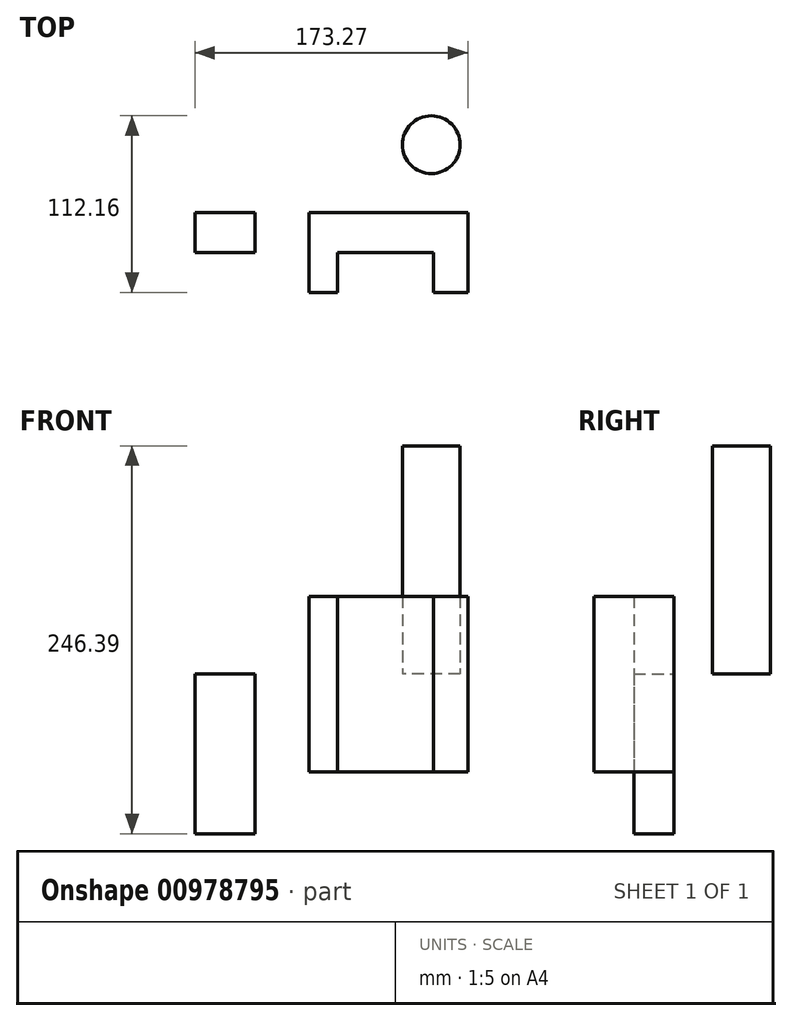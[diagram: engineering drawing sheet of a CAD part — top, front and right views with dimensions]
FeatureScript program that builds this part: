
annotation { "Feature Type Name" : "Feature", "Feature Type Description" : "" }
export const myFeature = defineFeature(function(context is Context, id is Id, definition is map)
    precondition{}
    {
        {
            var Q0;
            Q0=qCreatedBy(makeId("Front.planeOp"),FACE);
            var sketch = newSketch(context, id + "F0", { "sketchPlane" : qUnion([Q0])});
            skLineSegment(sketch, "E0.bottom", {"start": v(-48.02, 49.2) * mm, "end": v(52.96, 49.2) * mm});
            skLineSegment(sketch, "E0.top", {"start": v(-48.02, -62.25) * mm, "end": v(52.96, -62.25) * mm});
            skLineSegment(sketch, "E0.left", {"start": v(-48.02, 49.2) * mm, "end": v(-48.02, -62.25) * mm});
            skLineSegment(sketch, "E0.right", {"start": v(52.96, 49.2) * mm, "end": v(52.96, -62.25) * mm});
            skSolve(sketch);
        }
        {
            var Q0;
            Q0=makeQuery(id+"F0.imprint","IMPRINT",FACE,{"disambiguationData":[TD([[makeQuery(id+"F0.imprint","IMPRINT",EDGE,{"derivedFrom":sQuery(id+"F0.wireOp",EDGE,"E0.bottom")}),-1.0]])]});
            extrude(context, id + "F1", {"entities" : qUnion([Q0]), "depth" : 25.4 * mm, "offsetDistance" : 25.4 * mm});
        }
        {
            var Q0;
            Q0=qCreatedBy(makeId("Front.planeOp"),FACE);
            var sketch = newSketch(context, id + "F2", { "sketchPlane" : qUnion([Q0])});
            skLineSegment(sketch, "E1.bottom", {"start": v(-120.3, 0) * mm, "end": v(-82.19, 0) * mm});
            skLineSegment(sketch, "E1.top", {"start": v(-120.3, -101.67) * mm, "end": v(-82.19, -101.67) * mm});
            skLineSegment(sketch, "E1.left", {"start": v(-120.3, 0) * mm, "end": v(-120.3, -101.67) * mm});
            skLineSegment(sketch, "E1.right", {"start": v(-82.19, 0) * mm, "end": v(-82.19, -101.67) * mm});
            skSolve(sketch);
        }
        {
            var Q0;
            Q0=makeQuery(id+"F2.imprint","IMPRINT",FACE,{"disambiguationData":[TD([[makeQuery(id+"F2.imprint","IMPRINT",EDGE,{"derivedFrom":sQuery(id+"F2.wireOp",EDGE,"E1.bottom")}),-1.0]])]});
            extrude(context, id + "F3", {"entities" : qUnion([Q0]), "depth" : 25.4 * mm, "offsetDistance" : 25.4 * mm});
        }
        {
            var Q0;
            Q0=makeQuery(id+"F1.opExtrude","CAP_FACE",FACE,{"disambiguationData":[OSD([sQuery(id+"F0.wireOp",EDGE,"E0.bottom"),sQuery(id+"F0.wireOp",EDGE,"E0.top"),sQuery(id+"F0.wireOp",EDGE,"E0.left"),sQuery(id+"F0.wireOp",EDGE,"E0.right")])],"isStart":false});
            var sketch = newSketch(context, id + "F4", { "sketchPlane" : qUnion([Q0])});
            skLineSegment(sketch, "E2", {"start": v(-29.89, 49.2) * mm, "end": v(-29.89, -62.25) * mm});
            skLineSegment(sketch, "E3", {"start": v(31.1, 49.2) * mm, "end": v(31.1, -62.25) * mm});
            skSolve(sketch);
        }
        {
            var Q0;
            {var subQ0=sQuery(id+"F4.wireOp",EDGE,"E3");Q0=makeQuery(id+"F4.imprint","IMPRINT",FACE,{"disambiguationData":[TD([[makeQuery(id+"F4.imprint","IMPRINT",EDGE,{"derivedFrom":subQ0}),1.0]])]});}
            var Q1;
            {var subQ0=sQuery(id+"F4.wireOp",EDGE,"E2");Q1=makeQuery(id+"F4.imprint","IMPRINT",FACE,{"disambiguationData":[TD([[makeQuery(id+"F4.imprint","IMPRINT",EDGE,{"derivedFrom":subQ0}),-1.0]])]});}
            extrude(context, id + "F5", {"entities" : qUnion([Q0, Q1]), "operationType" : NewBodyOperationType.ADD, "depth" : 25.4 * mm, "offsetDistance" : 25.4 * mm});
        }
        {
            var Q0;
            Q0=qCreatedBy(makeId("Top.planeOp"),FACE);
            var sketch = newSketch(context, id + "F6", { "sketchPlane" : qUnion([Q0])});
            skCircle(sketch, "E4", {"center": v(29.75, 43) * mm, "radius": 18.37 * mm});
            skSolve(sketch);
        }
        {
            var Q0;
            Q0=makeQuery(id+"F6.imprint","IMPRINT",FACE,{"disambiguationData":[TD([[makeQuery(id+"F6.imprint","IMPRINT",EDGE,{"derivedFrom":sQuery(id+"F6.wireOp",EDGE,"E4")}),1.0]])]});
            extrude(context, id + "F7", {"entities" : qUnion([Q0]), "depth" : 144.72 * mm, "offsetDistance" : 25.4 * mm});
        }
    });
